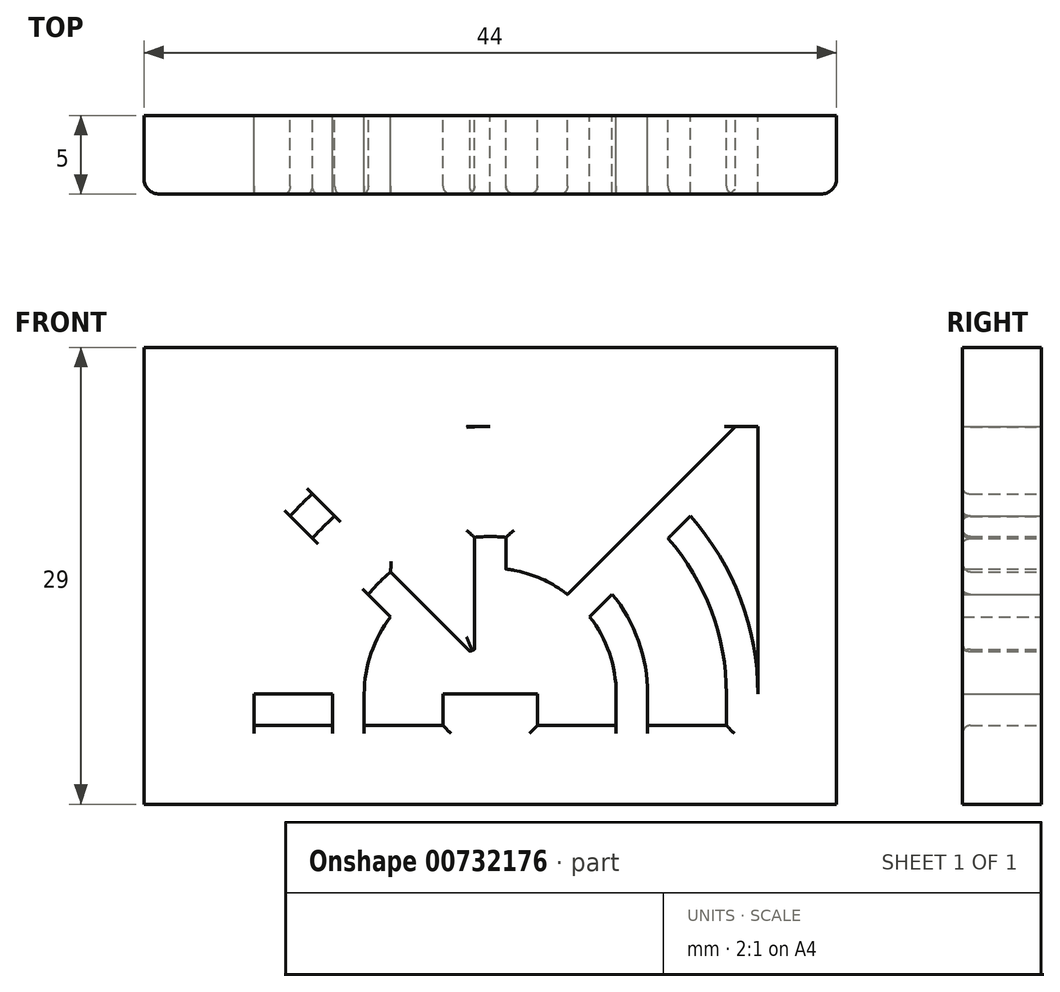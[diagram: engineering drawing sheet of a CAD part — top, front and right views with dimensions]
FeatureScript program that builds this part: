
annotation { "Feature Type Name" : "Feature", "Feature Type Description" : "" }
export const myFeature = defineFeature(function(context is Context, id is Id, definition is map)
    precondition{}
    {
        {
            var Q0;
            Q0=qCreatedBy(makeId("Front.planeOp"),FACE);
            var sketch = newSketch(context, id + "F0", { "sketchPlane" : qUnion([Q0])});
            skLineSegment(sketch, "E0.bottom", {"start": v(44, 28.95) * mm, "end": v(0, 28.95) * mm});
            skLineSegment(sketch, "E0.top", {"start": v(44, -0.05) * mm, "end": v(0, -0.05) * mm});
            skLineSegment(sketch, "E0.left", {"start": v(44, 28.95) * mm, "end": v(44, -0.05) * mm});
            skLineSegment(sketch, "E0.right", {"start": v(0, 28.95) * mm, "end": v(0, -0.05) * mm});
            skPoint(sketch, "E1.middle", {"position": v(22, 14.45) * mm});
            skLineSegment(sketch, "E2", {"start": v(5, 6.95) * mm, "end": v(39, 6.95) * mm});
            skPoint(sketch, "E3", {"position": v(22, 6.95) * mm});
            skArc(sketch, "E4", {"start": v(5, 6.95) * mm, "mid": v(22, 23.95) * mm, "end": v(39, 6.95) * mm});
            skArc(sketch, "E5", {"start": v(7, 6.95) * mm, "mid": v(22, 21.95) * mm, "end": v(37, 6.95) * mm});
            skArc(sketch, "E6", {"start": v(12, 6.95) * mm, "mid": v(22, 16.95) * mm, "end": v(32, 6.95) * mm});
            skArc(sketch, "E7", {"start": v(14, 6.95) * mm, "mid": v(22, 14.95) * mm, "end": v(30, 6.95) * mm});
            skArc(sketch, "E8", {"start": v(19, 6.95) * mm, "mid": v(22, 9.95) * mm, "end": v(25, 6.95) * mm});
            skLineSegment(sketch, "E9", {"start": v(7, 6.95) * mm, "end": v(7, 4.95) * mm});
            skLineSegment(sketch, "E10", {"start": v(12, 6.95) * mm, "end": v(12, 4.95) * mm});
            skLineSegment(sketch, "E11", {"start": v(14, 6.95) * mm, "end": v(14, 4.95) * mm});
            skLineSegment(sketch, "E12", {"start": v(19, 6.95) * mm, "end": v(19, 4.95) * mm});
            skLineSegment(sketch, "E13", {"start": v(25, 6.95) * mm, "end": v(25, 4.95) * mm});
            skLineSegment(sketch, "E14", {"start": v(30, 6.95) * mm, "end": v(30, 4.95) * mm});
            skLineSegment(sketch, "E15", {"start": v(32, 6.95) * mm, "end": v(32, 4.95) * mm});
            skLineSegment(sketch, "E16", {"start": v(37, 6.95) * mm, "end": v(37, 4.95) * mm});
            skLineSegment(sketch, "E17", {"start": v(37.59, 23.95) * mm, "end": v(23.3, 9.66) * mm});
            skLineSegment(sketch, "E18", {"start": v(39, 22.53) * mm, "end": v(24.7, 8.24) * mm});
            skLineSegment(sketch, "E19", {"start": v(21, 23.92) * mm, "end": v(21, 9.78) * mm});
            skLineSegment(sketch, "E20", {"start": v(23, 23.92) * mm, "end": v(23, 9.78) * mm});
            skLineSegment(sketch, "E21", {"start": v(6.41, 23.95) * mm, "end": v(20.7, 9.66) * mm});
            skLineSegment(sketch, "E22", {"start": v(5, 22.53) * mm, "end": v(19.3, 8.24) * mm});
            skLineSegment(sketch, "E23", {"start": v(5, 23.95) * mm, "end": v(39, 23.95) * mm});
            skLineSegment(sketch, "E24", {"start": v(5, 23.95) * mm, "end": v(5, 4.95) * mm});
            skLineSegment(sketch, "E25", {"start": v(39, 23.95) * mm, "end": v(39, 4.95) * mm});
            skLineSegment(sketch, "E26", {"start": v(5, 4.95) * mm, "end": v(39, 4.95) * mm});
            skLineSegment(sketch, "E27", {"start": v(21, 23.87) * mm, "end": v(21, 23.95) * mm});
            skLineSegment(sketch, "E28", {"start": v(23, 23.86) * mm, "end": v(23, 23.95) * mm});
            skSolve(sketch);
        }
        {
            var Q0;
            {var subQ5=sQuery(id+"F0.wireOp",EDGE,"E27");var subQ7=sQuery(id+"F0.wireOp",EDGE,"E4");var subQ11=makeQuery(id+"F0.imprint","INTERSECT",VERTEX,{"derivedFrom":[subQ7,subQ5]});Q0=makeQuery(id+"F0.imprint","IMPRINT",FACE,{"disambiguationData":[TD([[makeQuery(id+"F0.imprint","IMPRINT",EDGE,{"disambiguationData":[TD([[subQ11,-1.0]])],"derivedFrom":subQ7}),-1.0]])]});}
            var Q1;
            {var subQ0=sQuery(id+"F0.wireOp",EDGE,"E19");var subQ1=sQuery(id+"F0.wireOp",EDGE,"E5");var subQ2=makeQuery(id+"F0.imprint","INTERSECT",VERTEX,{"derivedFrom":[subQ1,subQ0]});Q1=makeQuery(id+"F0.imprint","IMPRINT",FACE,{"disambiguationData":[TD([[makeQuery(id+"F0.imprint","IMPRINT",EDGE,{"disambiguationData":[TD([[subQ2,-1.0]])],"derivedFrom":subQ1}),-1.0]])]});}
            var Q2;
            Q2=makeQuery(id+"F0.imprint","IMPRINT",FACE,{"disambiguationData":[TD([[makeQuery(id+"F0.imprint","IMPRINT",EDGE,{"derivedFrom":sQuery(id+"F0.wireOp",EDGE,"E0.bottom")}),1.0]])]});
            var Q3;
            {var subQ5=sQuery(id+"F0.wireOp",EDGE,"E22");var subQ7=sQuery(id+"F0.wireOp",EDGE,"E4");var subQ8=makeQuery(id+"F0.imprint","INTERSECT",VERTEX,{"derivedFrom":[subQ7,subQ5]});Q3=makeQuery(id+"F0.imprint","IMPRINT",FACE,{"disambiguationData":[TD([[makeQuery(id+"F0.imprint","IMPRINT",EDGE,{"disambiguationData":[TD([[subQ8,-1.0]])],"derivedFrom":subQ7}),1.0]])]});}
            var Q4;
            {var subQ0=sQuery(id+"F0.wireOp",EDGE,"E22");var subQ1=sQuery(id+"F0.wireOp",EDGE,"E4");var subQ2=makeQuery(id+"F0.imprint","INTERSECT",VERTEX,{"derivedFrom":[subQ1,subQ0]});Q4=makeQuery(id+"F0.imprint","IMPRINT",FACE,{"disambiguationData":[TD([[makeQuery(id+"F0.imprint","IMPRINT",EDGE,{"disambiguationData":[TD([[subQ2,-1.0]])],"derivedFrom":subQ1}),-1.0]])]});}
            var Q5;
            {var subQ0=sQuery(id+"F0.wireOp",EDGE,"E21");var subQ1=sQuery(id+"F0.wireOp",EDGE,"E4");var subQ2=makeQuery(id+"F0.imprint","INTERSECT",VERTEX,{"derivedFrom":[subQ1,subQ0]});Q5=makeQuery(id+"F0.imprint","IMPRINT",FACE,{"disambiguationData":[TD([[makeQuery(id+"F0.imprint","IMPRINT",EDGE,{"disambiguationData":[TD([[subQ2,-1.0]])],"derivedFrom":subQ1}),-1.0]])]});}
            var Q6;
            {var subQ0=sQuery(id+"F0.wireOp",EDGE,"E4");var subQ5=sQuery(id+"F0.wireOp",EDGE,"E22");var subQ6=makeQuery(id+"F0.imprint","INTERSECT",VERTEX,{"derivedFrom":[subQ0,subQ5]});Q6=makeQuery(id+"F0.imprint","IMPRINT",FACE,{"disambiguationData":[TD([[makeQuery(id+"F0.imprint","IMPRINT",EDGE,{"disambiguationData":[TD([[subQ6,-1.0]])],"derivedFrom":subQ5}),-1.0]])]});}
            var Q7;
            {var subQ3=sQuery(id+"F0.wireOp",EDGE,"E9");Q7=makeQuery(id+"F0.imprint","IMPRINT",FACE,{"disambiguationData":[TD([[makeQuery(id+"F0.imprint","IMPRINT",EDGE,{"derivedFrom":subQ3}),-1.0]])]});}
            var Q8;
            {var subQ0=sQuery(id+"F0.wireOp",EDGE,"E10");Q8=makeQuery(id+"F0.imprint","IMPRINT",FACE,{"disambiguationData":[TD([[makeQuery(id+"F0.imprint","IMPRINT",EDGE,{"derivedFrom":subQ0}),1.0]])]});}
            var Q9;
            {var subQ0=sQuery(id+"F0.wireOp",EDGE,"E6");var subQ5=sQuery(id+"F0.wireOp",EDGE,"E22");var subQ6=makeQuery(id+"F0.imprint","INTERSECT",VERTEX,{"derivedFrom":[subQ0,subQ5]});Q9=makeQuery(id+"F0.imprint","IMPRINT",FACE,{"disambiguationData":[TD([[makeQuery(id+"F0.imprint","IMPRINT",EDGE,{"disambiguationData":[TD([[subQ6,-1.0]])],"derivedFrom":subQ5}),-1.0]])]});}
            var Q10;
            {var subQ0=sQuery(id+"F0.wireOp",EDGE,"E22");var subQ1=sQuery(id+"F0.wireOp",EDGE,"E6");var subQ2=makeQuery(id+"F0.imprint","INTERSECT",VERTEX,{"derivedFrom":[subQ1,subQ0]});Q10=makeQuery(id+"F0.imprint","IMPRINT",FACE,{"disambiguationData":[TD([[makeQuery(id+"F0.imprint","IMPRINT",EDGE,{"disambiguationData":[TD([[subQ2,-1.0]])],"derivedFrom":subQ1}),-1.0]])]});}
            var Q11;
            {var subQ0=sQuery(id+"F0.wireOp",EDGE,"E22");var subQ1=sQuery(id+"F0.wireOp",EDGE,"E5");var subQ2=makeQuery(id+"F0.imprint","INTERSECT",VERTEX,{"derivedFrom":[subQ1,subQ0]});Q11=makeQuery(id+"F0.imprint","IMPRINT",FACE,{"disambiguationData":[TD([[makeQuery(id+"F0.imprint","IMPRINT",EDGE,{"disambiguationData":[TD([[subQ2,-1.0]])],"derivedFrom":subQ1}),-1.0]])]});}
            var Q12;
            {var subQ0=sQuery(id+"F0.wireOp",EDGE,"E21");var subQ1=sQuery(id+"F0.wireOp",EDGE,"E6");var subQ2=makeQuery(id+"F0.imprint","INTERSECT",VERTEX,{"derivedFrom":[subQ1,subQ0]});Q12=makeQuery(id+"F0.imprint","IMPRINT",FACE,{"disambiguationData":[TD([[makeQuery(id+"F0.imprint","IMPRINT",EDGE,{"disambiguationData":[TD([[subQ2,-1.0]])],"derivedFrom":subQ1}),-1.0]])]});}
            var Q13;
            {var subQ0=sQuery(id+"F0.wireOp",EDGE,"E28");var subQ7=sQuery(id+"F0.wireOp",EDGE,"E4");var subQ9=makeQuery(id+"F0.imprint","INTERSECT",VERTEX,{"derivedFrom":[subQ7,subQ0]});Q13=makeQuery(id+"F0.imprint","IMPRINT",FACE,{"disambiguationData":[TD([[makeQuery(id+"F0.imprint","IMPRINT",EDGE,{"disambiguationData":[TD([[subQ9,-1.0]])],"derivedFrom":subQ7}),-1.0]])]});}
            var Q14;
            {var subQ1=sQuery(id+"F0.wireOp",EDGE,"E17");var subQ5=sQuery(id+"F0.wireOp",EDGE,"E4");var subQ6=makeQuery(id+"F0.imprint","INTERSECT",VERTEX,{"derivedFrom":[subQ5,subQ1]});Q14=makeQuery(id+"F0.imprint","IMPRINT",FACE,{"disambiguationData":[TD([[makeQuery(id+"F0.imprint","IMPRINT",EDGE,{"disambiguationData":[TD([[subQ6,-1.0]])],"derivedFrom":subQ5}),1.0]])]});}
            var Q15;
            {var subQ0=sQuery(id+"F0.wireOp",EDGE,"E17");var subQ1=sQuery(id+"F0.wireOp",EDGE,"E4");var subQ2=makeQuery(id+"F0.imprint","INTERSECT",VERTEX,{"derivedFrom":[subQ1,subQ0]});Q15=makeQuery(id+"F0.imprint","IMPRINT",FACE,{"disambiguationData":[TD([[makeQuery(id+"F0.imprint","IMPRINT",EDGE,{"disambiguationData":[TD([[subQ2,-1.0]])],"derivedFrom":subQ1}),-1.0]])]});}
            var Q16;
            {var subQ0=sQuery(id+"F0.wireOp",EDGE,"E17");var subQ1=sQuery(id+"F0.wireOp",EDGE,"E5");var subQ2=makeQuery(id+"F0.imprint","INTERSECT",VERTEX,{"derivedFrom":[subQ1,subQ0]});Q16=makeQuery(id+"F0.imprint","IMPRINT",FACE,{"disambiguationData":[TD([[makeQuery(id+"F0.imprint","IMPRINT",EDGE,{"disambiguationData":[TD([[subQ2,-1.0]])],"derivedFrom":subQ1}),-1.0]])]});}
            var Q17;
            {var subQ0=sQuery(id+"F0.wireOp",EDGE,"E4");var subQ5=sQuery(id+"F0.wireOp",EDGE,"E18");var subQ7=makeQuery(id+"F0.imprint","INTERSECT",VERTEX,{"derivedFrom":[subQ0,subQ5]});Q17=makeQuery(id+"F0.imprint","IMPRINT",FACE,{"disambiguationData":[TD([[makeQuery(id+"F0.imprint","IMPRINT",EDGE,{"disambiguationData":[TD([[subQ7,-1.0]])],"derivedFrom":subQ5}),1.0]])]});}
            var Q18;
            {var subQ3=sQuery(id+"F0.wireOp",EDGE,"E16");Q18=makeQuery(id+"F0.imprint","IMPRINT",FACE,{"disambiguationData":[TD([[makeQuery(id+"F0.imprint","IMPRINT",EDGE,{"derivedFrom":subQ3}),1.0]])]});}
            var Q19;
            {var subQ0=sQuery(id+"F0.wireOp",EDGE,"E6");var subQ5=sQuery(id+"F0.wireOp",EDGE,"E18");var subQ6=makeQuery(id+"F0.imprint","INTERSECT",VERTEX,{"derivedFrom":[subQ0,subQ5]});Q19=makeQuery(id+"F0.imprint","IMPRINT",FACE,{"disambiguationData":[TD([[makeQuery(id+"F0.imprint","IMPRINT",EDGE,{"disambiguationData":[TD([[subQ6,-1.0]])],"derivedFrom":subQ5}),1.0]])]});}
            var Q20;
            {var subQ0=sQuery(id+"F0.wireOp",EDGE,"E17");var subQ1=sQuery(id+"F0.wireOp",EDGE,"E6");var subQ2=makeQuery(id+"F0.imprint","INTERSECT",VERTEX,{"derivedFrom":[subQ1,subQ0]});Q20=makeQuery(id+"F0.imprint","IMPRINT",FACE,{"disambiguationData":[TD([[makeQuery(id+"F0.imprint","IMPRINT",EDGE,{"disambiguationData":[TD([[subQ2,-1.0]])],"derivedFrom":subQ1}),-1.0]])]});}
            var Q21;
            {var subQ0=sQuery(id+"F0.wireOp",EDGE,"E20");var subQ1=sQuery(id+"F0.wireOp",EDGE,"E6");var subQ2=makeQuery(id+"F0.imprint","INTERSECT",VERTEX,{"derivedFrom":[subQ1,subQ0]});Q21=makeQuery(id+"F0.imprint","IMPRINT",FACE,{"disambiguationData":[TD([[makeQuery(id+"F0.imprint","IMPRINT",EDGE,{"disambiguationData":[TD([[subQ2,-1.0]])],"derivedFrom":subQ1}),-1.0]])]});}
            var Q22;
            {var subQ0=sQuery(id+"F0.wireOp",EDGE,"E27");var subQ1=sQuery(id+"F0.wireOp",EDGE,"E4");var subQ2=makeQuery(id+"F0.imprint","INTERSECT",VERTEX,{"derivedFrom":[subQ1,subQ0]});Q22=makeQuery(id+"F0.imprint","IMPRINT",FACE,{"disambiguationData":[TD([[makeQuery(id+"F0.imprint","IMPRINT",EDGE,{"disambiguationData":[TD([[subQ2,-1.0]])],"derivedFrom":subQ1}),1.0]])]});}
            var Q23;
            {var subQ0=sQuery(id+"F0.wireOp",EDGE,"E23");var subQ1=sQuery(id+"F0.wireOp",EDGE,"E4");var subQ2=makeQuery(id+"F0.imprint","INTERSECT",VERTEX,{"derivedFrom":[subQ1,subQ0]});Q23=makeQuery(id+"F0.imprint","IMPRINT",FACE,{"disambiguationData":[TD([[makeQuery(id+"F0.imprint","IMPRINT",EDGE,{"disambiguationData":[TD([[subQ2,-1.0]])],"derivedFrom":subQ1}),1.0]])]});}
            var Q24;
            {var subQ2=sQuery(id+"F0.wireOp",EDGE,"E14");Q24=makeQuery(id+"F0.imprint","IMPRINT",FACE,{"disambiguationData":[TD([[makeQuery(id+"F0.imprint","IMPRINT",EDGE,{"derivedFrom":subQ2}),1.0]])]});}
            var Q25;
            {var subQ0=sQuery(id+"F0.wireOp",EDGE,"E19");var subQ1=sQuery(id+"F0.wireOp",EDGE,"E6");var subQ2=makeQuery(id+"F0.imprint","INTERSECT",VERTEX,{"derivedFrom":[subQ1,subQ0]});Q25=makeQuery(id+"F0.imprint","IMPRINT",FACE,{"disambiguationData":[TD([[makeQuery(id+"F0.imprint","IMPRINT",EDGE,{"disambiguationData":[TD([[subQ2,-1.0]])],"derivedFrom":subQ1}),-1.0]])]});}
            var Q26;
            {var subQ0=sQuery(id+"F0.wireOp",EDGE,"E19");var subQ1=sQuery(id+"F0.wireOp",EDGE,"E7");var subQ2=makeQuery(id+"F0.imprint","INTERSECT",VERTEX,{"derivedFrom":[subQ1,subQ0]});Q26=makeQuery(id+"F0.imprint","IMPRINT",FACE,{"disambiguationData":[TD([[makeQuery(id+"F0.imprint","IMPRINT",EDGE,{"disambiguationData":[TD([[subQ2,-1.0]])],"derivedFrom":subQ1}),-1.0]])]});}
            var Q27;
            {var subQ0=sQuery(id+"F0.wireOp",EDGE,"E17");var subQ1=sQuery(id+"F0.wireOp",EDGE,"E7");var subQ2=makeQuery(id+"F0.imprint","INTERSECT",VERTEX,{"derivedFrom":[subQ1,subQ0]});Q27=makeQuery(id+"F0.imprint","IMPRINT",FACE,{"disambiguationData":[TD([[makeQuery(id+"F0.imprint","IMPRINT",EDGE,{"disambiguationData":[TD([[subQ2,-1.0]])],"derivedFrom":subQ1}),-1.0]])]});}
            var Q28;
            {var subQ0=sQuery(id+"F0.wireOp",EDGE,"E22");var subQ1=sQuery(id+"F0.wireOp",EDGE,"E7");var subQ2=makeQuery(id+"F0.imprint","INTERSECT",VERTEX,{"derivedFrom":[subQ1,subQ0]});Q28=makeQuery(id+"F0.imprint","IMPRINT",FACE,{"disambiguationData":[TD([[makeQuery(id+"F0.imprint","IMPRINT",EDGE,{"disambiguationData":[TD([[subQ2,-1.0]])],"derivedFrom":subQ1}),-1.0]])]});}
            var Q29;
            {var subQ0=sQuery(id+"F0.wireOp",EDGE,"E8");var subQ2=makeQuery(id+"F0.imprint","INTERSECT",VERTEX,{"derivedFrom":[subQ0,sQuery(id+"F0.wireOp",EDGE,"E21")]});Q29=makeQuery(id+"F0.imprint","IMPRINT",FACE,{"disambiguationData":[TD([[makeQuery(id+"F0.imprint","IMPRINT",EDGE,{"disambiguationData":[TD([[subQ2,1.0]])],"derivedFrom":subQ0}),-1.0]])]});}
            var Q30;
            {var subQ0=sQuery(id+"F0.wireOp",EDGE,"E12");Q30=makeQuery(id+"F0.imprint","IMPRINT",FACE,{"disambiguationData":[TD([[makeQuery(id+"F0.imprint","IMPRINT",EDGE,{"derivedFrom":subQ0}),1.0]])]});}
            extrude(context, id + "F1", {"entities" : qUnion([Q0, Q1, Q2, Q3, Q4, Q5, Q6, Q7, Q8, Q9, Q10, Q11, Q12, Q13, Q14, Q15, Q16, Q17, Q18, Q19, Q20, Q21, Q22, Q23, Q24, Q25, Q26, Q27, Q28, Q29, Q30]), "depth" : 5 * mm, "offsetDistance" : 25 * mm});
        }
        {
            var Q0;
            {var subQ0=sQuery(id+"F0.wireOp",EDGE,"E5");Q0=makeQuery(id+"F1.opExtrude","CAP_EDGE",EDGE,{"disambiguationData":[OSD([subQ0]),TDD([makeQuery(id+"F0.imprint","IMPRINT",EDGE,{"disambiguationData":[TD([[makeQuery(id+"F0.imprint","INTERSECT",VERTEX,{"derivedFrom":[subQ0,sQuery(id+"F0.wireOp",EDGE,"E22")]}),1.0]])],"derivedFrom":subQ0})])],"isStart":false});}
            var Q1;
            {var subQ0=sQuery(id+"F0.wireOp",EDGE,"E22");Q1=makeQuery(id+"F1.opExtrude","CAP_EDGE",EDGE,{"disambiguationData":[OSD([subQ0]),TDD([makeQuery(id+"F0.imprint","IMPRINT",EDGE,{"disambiguationData":[TD([[makeQuery(id+"F0.imprint","INTERSECT",VERTEX,{"derivedFrom":[sQuery(id+"F0.wireOp",EDGE,"E5"),subQ0]}),-1.0]])],"derivedFrom":subQ0})])],"isStart":false});}
            var Q2;
            {var subQ0=sQuery(id+"F0.wireOp",EDGE,"E19");Q2=makeQuery(id+"F1.opExtrude","CAP_EDGE",EDGE,{"disambiguationData":[OSD([subQ0]),TDD([makeQuery(id+"F0.imprint","IMPRINT",EDGE,{"disambiguationData":[TD([[makeQuery(id+"F0.imprint","INTERSECT",VERTEX,{"derivedFrom":[sQuery(id+"F0.wireOp",EDGE,"E5"),subQ0]}),-1.0]])],"derivedFrom":subQ0})])],"isStart":false});}
            var Q3;
            {var subQ0=sQuery(id+"F0.wireOp",EDGE,"E6");Q3=makeQuery(id+"F1.opExtrude","CAP_EDGE",EDGE,{"disambiguationData":[OSD([subQ0]),TDD([makeQuery(id+"F0.imprint","IMPRINT",EDGE,{"disambiguationData":[TD([[makeQuery(id+"F0.imprint","INTERSECT",VERTEX,{"derivedFrom":[subQ0,sQuery(id+"F0.wireOp",EDGE,"E21")]}),-1.0]])],"derivedFrom":subQ0})])],"isStart":false});}
            var Q4;
            {var subQ0=sQuery(id+"F0.wireOp",EDGE,"E5");Q4=makeQuery(id+"F1.opExtrude","CAP_EDGE",EDGE,{"disambiguationData":[OSD([subQ0]),TDD([makeQuery(id+"F0.imprint","IMPRINT",EDGE,{"disambiguationData":[TD([[makeQuery(id+"F0.imprint","INTERSECT",VERTEX,{"derivedFrom":[subQ0,sQuery(id+"F0.wireOp",EDGE,"E21")]}),-1.0]])],"derivedFrom":subQ0})])],"isStart":false});}
            var Q5;
            {var subQ0=sQuery(id+"F0.wireOp",EDGE,"E21");Q5=makeQuery(id+"F1.opExtrude","CAP_EDGE",EDGE,{"disambiguationData":[OSD([subQ0]),TDD([makeQuery(id+"F0.imprint","IMPRINT",EDGE,{"disambiguationData":[TD([[makeQuery(id+"F0.imprint","INTERSECT",VERTEX,{"derivedFrom":[sQuery(id+"F0.wireOp",EDGE,"E5"),subQ0]}),-1.0]])],"derivedFrom":subQ0})])],"isStart":false});}
            var Q6;
            {var subQ0=sQuery(id+"F0.wireOp",EDGE,"E6");Q6=makeQuery(id+"F1.opExtrude","CAP_EDGE",EDGE,{"disambiguationData":[OSD([subQ0]),TDD([makeQuery(id+"F0.imprint","IMPRINT",EDGE,{"disambiguationData":[TD([[makeQuery(id+"F0.imprint","INTERSECT",VERTEX,{"derivedFrom":[subQ0,sQuery(id+"F0.wireOp",EDGE,"E22")]}),1.0]])],"derivedFrom":subQ0})])],"isStart":false});}
            var Q7;
            {var subQ0=sQuery(id+"F0.wireOp",EDGE,"E7");Q7=makeQuery(id+"F1.opExtrude","CAP_EDGE",EDGE,{"disambiguationData":[OSD([subQ0]),TDD([makeQuery(id+"F0.imprint","IMPRINT",EDGE,{"disambiguationData":[TD([[makeQuery(id+"F0.imprint","INTERSECT",VERTEX,{"derivedFrom":[subQ0,sQuery(id+"F0.wireOp",EDGE,"E22")]}),1.0]])],"derivedFrom":subQ0})])],"isStart":false});}
            var Q8;
            Q8=makeQuery(id+"F1.opExtrude","CAP_EDGE",EDGE,{"disambiguationData":[OSD([sQuery(id+"F0.wireOp",EDGE,"E12")])],"isStart":false});
            var Q9;
            {var subQ0=sQuery(id+"F0.wireOp",EDGE,"E8");Q9=makeQuery(id+"F1.opExtrude","CAP_EDGE",EDGE,{"disambiguationData":[OSD([subQ0]),TDD([makeQuery(id+"F0.imprint","IMPRINT",EDGE,{"disambiguationData":[TD([[makeQuery(id+"F0.imprint","INTERSECT",VERTEX,{"derivedFrom":[subQ0,sQuery(id+"F0.wireOp",EDGE,"E22")]}),1.0]])],"derivedFrom":subQ0})])],"isStart":false});}
            var Q10;
            {var subQ0=sQuery(id+"F0.wireOp",EDGE,"E22");Q10=makeQuery(id+"F1.opExtrude","CAP_EDGE",EDGE,{"disambiguationData":[OSD([subQ0]),TDD([makeQuery(id+"F0.imprint","IMPRINT",EDGE,{"disambiguationData":[TD([[makeQuery(id+"F0.imprint","INTERSECT",VERTEX,{"derivedFrom":[sQuery(id+"F0.wireOp",EDGE,"E8"),subQ0]}),1.0]])],"derivedFrom":subQ0})])],"isStart":false});}
            var Q11;
            {var subQ0=sQuery(id+"F0.wireOp",EDGE,"E4");Q11=makeQuery(id+"F1.opExtrude","CAP_EDGE",EDGE,{"disambiguationData":[OSD([subQ0]),TDD([makeQuery(id+"F0.imprint","IMPRINT",EDGE,{"disambiguationData":[TD([[makeQuery(id+"F0.imprint","INTERSECT",VERTEX,{"derivedFrom":[subQ0,sQuery(id+"F0.wireOp",EDGE,"E21")]}),-1.0]])],"derivedFrom":subQ0})])],"isStart":false});}
            var Q12;
            {var subQ0=sQuery(id+"F0.wireOp",EDGE,"E23");Q12=makeQuery(id+"F1.opExtrude","CAP_EDGE",EDGE,{"disambiguationData":[OSD([subQ0]),TDD([makeQuery(id+"F0.imprint","IMPRINT",EDGE,{"disambiguationData":[TD([[makeQuery(id+"F0.imprint","INTERSECT",VERTEX,{"derivedFrom":[sQuery(id+"F0.wireOp",EDGE,"E21"),subQ0]}),-1.0]])],"derivedFrom":subQ0})])],"isStart":false});}
            var Q13;
            {var subQ0=sQuery(id+"F0.wireOp",EDGE,"E21");Q13=makeQuery(id+"F1.opExtrude","CAP_EDGE",EDGE,{"disambiguationData":[OSD([subQ0]),TDD([makeQuery(id+"F0.imprint","IMPRINT",EDGE,{"disambiguationData":[TD([[makeQuery(id+"F0.imprint","INTERSECT",VERTEX,{"derivedFrom":[subQ0,sQuery(id+"F0.wireOp",EDGE,"E23")]}),-1.0]])],"derivedFrom":subQ0})])],"isStart":false});}
            var Q14;
            {var subQ0=sQuery(id+"F0.wireOp",EDGE,"E21");Q14=makeQuery(id+"F1.opExtrude","CAP_EDGE",EDGE,{"disambiguationData":[OSD([subQ0]),TDD([makeQuery(id+"F0.imprint","IMPRINT",EDGE,{"disambiguationData":[TD([[makeQuery(id+"F0.imprint","INTERSECT",VERTEX,{"derivedFrom":[sQuery(id+"F0.wireOp",EDGE,"E8"),subQ0]}),1.0]])],"derivedFrom":subQ0})])],"isStart":false});}
            var Q15;
            {var subQ0=sQuery(id+"F0.wireOp",EDGE,"E7");Q15=makeQuery(id+"F1.opExtrude","CAP_EDGE",EDGE,{"disambiguationData":[OSD([subQ0]),TDD([makeQuery(id+"F0.imprint","IMPRINT",EDGE,{"disambiguationData":[TD([[makeQuery(id+"F0.imprint","INTERSECT",VERTEX,{"derivedFrom":[subQ0,sQuery(id+"F0.wireOp",EDGE,"E21")]}),-1.0]])],"derivedFrom":subQ0})])],"isStart":false});}
            var Q16;
            {var subQ0=sQuery(id+"F0.wireOp",EDGE,"E19");Q16=makeQuery(id+"F1.opExtrude","CAP_EDGE",EDGE,{"disambiguationData":[OSD([subQ0]),TDD([makeQuery(id+"F0.imprint","IMPRINT",EDGE,{"disambiguationData":[TD([[makeQuery(id+"F0.imprint","INTERSECT",VERTEX,{"derivedFrom":[sQuery(id+"F0.wireOp",EDGE,"E8"),subQ0]}),1.0]])],"derivedFrom":subQ0})])],"isStart":false});}
            var Q17;
            {var subQ0=sQuery(id+"F0.wireOp",EDGE,"E20");Q17=makeQuery(id+"F1.opExtrude","CAP_EDGE",EDGE,{"disambiguationData":[OSD([subQ0]),TDD([makeQuery(id+"F0.imprint","IMPRINT",EDGE,{"disambiguationData":[TD([[makeQuery(id+"F0.imprint","INTERSECT",VERTEX,{"derivedFrom":[sQuery(id+"F0.wireOp",EDGE,"E5"),subQ0]}),-1.0]])],"derivedFrom":subQ0})])],"isStart":false});}
            var Q18;
            {var subQ0=sQuery(id+"F0.wireOp",EDGE,"E5");Q18=makeQuery(id+"F1.opExtrude","CAP_EDGE",EDGE,{"disambiguationData":[OSD([subQ0]),TDD([makeQuery(id+"F0.imprint","IMPRINT",EDGE,{"disambiguationData":[TD([[makeQuery(id+"F0.imprint","INTERSECT",VERTEX,{"derivedFrom":[subQ0,sQuery(id+"F0.wireOp",EDGE,"E20")]}),-1.0]])],"derivedFrom":subQ0})])],"isStart":false});}
            var Q19;
            {var subQ0=sQuery(id+"F0.wireOp",EDGE,"E23");Q19=makeQuery(id+"F1.opExtrude","CAP_EDGE",EDGE,{"disambiguationData":[OSD([subQ0]),TDD([makeQuery(id+"F0.imprint","IMPRINT",EDGE,{"disambiguationData":[TD([[makeQuery(id+"F0.imprint","INTERSECT",VERTEX,{"derivedFrom":[sQuery(id+"F0.wireOp",EDGE,"E17"),subQ0]}),1.0]])],"derivedFrom":subQ0})])],"isStart":false});}
            var Q20;
            {var subQ0=sQuery(id+"F0.wireOp",EDGE,"E17");Q20=makeQuery(id+"F1.opExtrude","CAP_EDGE",EDGE,{"disambiguationData":[OSD([subQ0]),TDD([makeQuery(id+"F0.imprint","IMPRINT",EDGE,{"disambiguationData":[TD([[makeQuery(id+"F0.imprint","INTERSECT",VERTEX,{"derivedFrom":[subQ0,sQuery(id+"F0.wireOp",EDGE,"E23")]}),-1.0]])],"derivedFrom":subQ0})])],"isStart":false});}
            var Q21;
            {var subQ0=sQuery(id+"F0.wireOp",EDGE,"E4");Q21=makeQuery(id+"F1.opExtrude","CAP_EDGE",EDGE,{"disambiguationData":[OSD([subQ0]),TDD([makeQuery(id+"F0.imprint","IMPRINT",EDGE,{"disambiguationData":[TD([[makeQuery(id+"F0.imprint","INTERSECT",VERTEX,{"derivedFrom":[subQ0,sQuery(id+"F0.wireOp",EDGE,"E28")]}),-1.0]])],"derivedFrom":subQ0})])],"isStart":false});}
            var Q22;
            {var subQ0=sQuery(id+"F0.wireOp",EDGE,"E22");Q22=makeQuery(id+"F1.opExtrude","CAP_EDGE",EDGE,{"disambiguationData":[OSD([subQ0]),TDD([makeQuery(id+"F0.imprint","IMPRINT",EDGE,{"disambiguationData":[TD([[makeQuery(id+"F0.imprint","INTERSECT",VERTEX,{"derivedFrom":[subQ0,sQuery(id+"F0.wireOp",EDGE,"E24")]}),-1.0]])],"derivedFrom":subQ0})])],"isStart":false});}
            var Q23;
            {var subQ0=sQuery(id+"F0.wireOp",EDGE,"E17");Q23=makeQuery(id+"F1.opExtrude","CAP_EDGE",EDGE,{"disambiguationData":[OSD([subQ0]),TDD([makeQuery(id+"F0.imprint","IMPRINT",EDGE,{"disambiguationData":[TD([[makeQuery(id+"F0.imprint","INTERSECT",VERTEX,{"derivedFrom":[sQuery(id+"F0.wireOp",EDGE,"E5"),subQ0]}),-1.0]])],"derivedFrom":subQ0})])],"isStart":false});}
            var Q24;
            {var subQ0=sQuery(id+"F0.wireOp",EDGE,"E6");Q24=makeQuery(id+"F1.opExtrude","CAP_EDGE",EDGE,{"disambiguationData":[OSD([subQ0]),TDD([makeQuery(id+"F0.imprint","IMPRINT",EDGE,{"disambiguationData":[TD([[makeQuery(id+"F0.imprint","INTERSECT",VERTEX,{"derivedFrom":[subQ0,sQuery(id+"F0.wireOp",EDGE,"E20")]}),-1.0]])],"derivedFrom":subQ0})])],"isStart":false});}
            var Q25;
            {var subQ0=sQuery(id+"F0.wireOp",EDGE,"E20");Q25=makeQuery(id+"F1.opExtrude","CAP_EDGE",EDGE,{"disambiguationData":[OSD([subQ0]),TDD([makeQuery(id+"F0.imprint","IMPRINT",EDGE,{"disambiguationData":[TD([[makeQuery(id+"F0.imprint","INTERSECT",VERTEX,{"derivedFrom":[sQuery(id+"F0.wireOp",EDGE,"E8"),subQ0]}),1.0]])],"derivedFrom":subQ0})])],"isStart":false});}
            var Q26;
            {var subQ0=sQuery(id+"F0.wireOp",EDGE,"E7");Q26=makeQuery(id+"F1.opExtrude","CAP_EDGE",EDGE,{"disambiguationData":[OSD([subQ0]),TDD([makeQuery(id+"F0.imprint","IMPRINT",EDGE,{"disambiguationData":[TD([[makeQuery(id+"F0.imprint","INTERSECT",VERTEX,{"derivedFrom":[subQ0,sQuery(id+"F0.wireOp",EDGE,"E20")]}),-1.0]])],"derivedFrom":subQ0})])],"isStart":false});}
            var Q27;
            {var subQ0=sQuery(id+"F0.wireOp",EDGE,"E17");Q27=makeQuery(id+"F1.opExtrude","CAP_EDGE",EDGE,{"disambiguationData":[OSD([subQ0]),TDD([makeQuery(id+"F0.imprint","IMPRINT",EDGE,{"disambiguationData":[TD([[makeQuery(id+"F0.imprint","INTERSECT",VERTEX,{"derivedFrom":[sQuery(id+"F0.wireOp",EDGE,"E8"),subQ0]}),1.0]])],"derivedFrom":subQ0})])],"isStart":false});}
            var Q28;
            {var subQ0=sQuery(id+"F0.wireOp",EDGE,"E18");Q28=makeQuery(id+"F1.opExtrude","CAP_EDGE",EDGE,{"disambiguationData":[OSD([subQ0]),TDD([makeQuery(id+"F0.imprint","IMPRINT",EDGE,{"disambiguationData":[TD([[makeQuery(id+"F0.imprint","INTERSECT",VERTEX,{"derivedFrom":[subQ0,sQuery(id+"F0.wireOp",EDGE,"E25")]}),-1.0]])],"derivedFrom":subQ0})])],"isStart":false});}
            var Q29;
            {var subQ0=sQuery(id+"F0.wireOp",EDGE,"E18");Q29=makeQuery(id+"F1.opExtrude","CAP_EDGE",EDGE,{"disambiguationData":[OSD([subQ0]),TDD([makeQuery(id+"F0.imprint","IMPRINT",EDGE,{"disambiguationData":[TD([[makeQuery(id+"F0.imprint","INTERSECT",VERTEX,{"derivedFrom":[sQuery(id+"F0.wireOp",EDGE,"E5"),subQ0]}),-1.0]])],"derivedFrom":subQ0})])],"isStart":false});}
            var Q30;
            {var subQ0=sQuery(id+"F0.wireOp",EDGE,"E5");Q30=makeQuery(id+"F1.opExtrude","CAP_EDGE",EDGE,{"disambiguationData":[OSD([subQ0]),TDD([makeQuery(id+"F0.imprint","IMPRINT",EDGE,{"disambiguationData":[TD([[makeQuery(id+"F0.imprint","INTERSECT",VERTEX,{"derivedFrom":[subQ0,sQuery(id+"F0.wireOp",EDGE,"E18")]}),-1.0]])],"derivedFrom":subQ0})])],"isStart":false});}
            var Q31;
            Q31=makeQuery(id+"F1.opExtrude","CAP_EDGE",EDGE,{"disambiguationData":[OSD([sQuery(id+"F0.wireOp",EDGE,"E16")])],"isStart":false});
            var Q32;
            {var subQ0=sQuery(id+"F0.wireOp",EDGE,"E26");Q32=makeQuery(id+"F1.opExtrude","CAP_EDGE",EDGE,{"disambiguationData":[OSD([subQ0]),TDD([makeQuery(id+"F0.imprint","IMPRINT",EDGE,{"disambiguationData":[TD([[makeQuery(id+"F0.imprint","INTERSECT",VERTEX,{"derivedFrom":[sQuery(id+"F0.wireOp",EDGE,"E15"),subQ0]}),-1.0]])],"derivedFrom":subQ0})])],"isStart":false});}
            var Q33;
            {var subQ0=sQuery(id+"F0.wireOp",EDGE,"E6");Q33=makeQuery(id+"F1.opExtrude","CAP_EDGE",EDGE,{"disambiguationData":[OSD([subQ0]),TDD([makeQuery(id+"F0.imprint","IMPRINT",EDGE,{"disambiguationData":[TD([[makeQuery(id+"F0.imprint","INTERSECT",VERTEX,{"derivedFrom":[subQ0,sQuery(id+"F0.wireOp",EDGE,"E18")]}),-1.0]])],"derivedFrom":subQ0})])],"isStart":false});}
            var Q34;
            {var subQ0=sQuery(id+"F0.wireOp",EDGE,"E7");Q34=makeQuery(id+"F1.opExtrude","CAP_EDGE",EDGE,{"disambiguationData":[OSD([subQ0]),TDD([makeQuery(id+"F0.imprint","IMPRINT",EDGE,{"disambiguationData":[TD([[makeQuery(id+"F0.imprint","INTERSECT",VERTEX,{"derivedFrom":[subQ0,sQuery(id+"F0.wireOp",EDGE,"E18")]}),-1.0]])],"derivedFrom":subQ0})])],"isStart":false});}
            var Q35;
            {var subQ0=sQuery(id+"F0.wireOp",EDGE,"E26");Q35=makeQuery(id+"F1.opExtrude","CAP_EDGE",EDGE,{"disambiguationData":[OSD([subQ0]),TDD([makeQuery(id+"F0.imprint","IMPRINT",EDGE,{"disambiguationData":[TD([[makeQuery(id+"F0.imprint","INTERSECT",VERTEX,{"derivedFrom":[sQuery(id+"F0.wireOp",EDGE,"E13"),subQ0]}),-1.0]])],"derivedFrom":subQ0})])],"isStart":false});}
            var Q36;
            {var subQ0=sQuery(id+"F0.wireOp",EDGE,"E18");Q36=makeQuery(id+"F1.opExtrude","CAP_EDGE",EDGE,{"disambiguationData":[OSD([subQ0]),TDD([makeQuery(id+"F0.imprint","IMPRINT",EDGE,{"disambiguationData":[TD([[makeQuery(id+"F0.imprint","INTERSECT",VERTEX,{"derivedFrom":[sQuery(id+"F0.wireOp",EDGE,"E8"),subQ0]}),1.0]])],"derivedFrom":subQ0})])],"isStart":false});}
            var Q37;
            Q37=makeQuery(id+"F1.opExtrude","CAP_EDGE",EDGE,{"disambiguationData":[OSD([sQuery(id+"F0.wireOp",EDGE,"E13")])],"isStart":false});
            var Q38;
            {var subQ0=sQuery(id+"F0.wireOp",EDGE,"E26");Q38=makeQuery(id+"F1.opExtrude","CAP_EDGE",EDGE,{"disambiguationData":[OSD([subQ0]),TDD([makeQuery(id+"F0.imprint","IMPRINT",EDGE,{"disambiguationData":[TD([[makeQuery(id+"F0.imprint","INTERSECT",VERTEX,{"derivedFrom":[sQuery(id+"F0.wireOp",EDGE,"E11"),subQ0]}),-1.0]])],"derivedFrom":subQ0})])],"isStart":false});}
            var Q39;
            {var subQ0=sQuery(id+"F0.wireOp",EDGE,"E26");Q39=makeQuery(id+"F1.opExtrude","CAP_EDGE",EDGE,{"disambiguationData":[OSD([subQ0]),TDD([makeQuery(id+"F0.imprint","IMPRINT",EDGE,{"disambiguationData":[TD([[makeQuery(id+"F0.imprint","INTERSECT",VERTEX,{"derivedFrom":[sQuery(id+"F0.wireOp",EDGE,"E9"),subQ0]}),-1.0]])],"derivedFrom":subQ0})])],"isStart":false});}
            var Q40;
            {var subQ0=sQuery(id+"F0.wireOp",EDGE,"E8");Q40=makeQuery(id+"F1.opExtrude","CAP_EDGE",EDGE,{"disambiguationData":[OSD([subQ0]),TDD([makeQuery(id+"F0.imprint","IMPRINT",EDGE,{"disambiguationData":[TD([[makeQuery(id+"F0.imprint","INTERSECT",VERTEX,{"derivedFrom":[subQ0,sQuery(id+"F0.wireOp",EDGE,"E19")]}),1.0]])],"derivedFrom":subQ0})])],"isStart":false});}
            var Q41;
            {var subQ0=sQuery(id+"F0.wireOp",EDGE,"E8");Q41=makeQuery(id+"F1.opExtrude","CAP_EDGE",EDGE,{"disambiguationData":[OSD([subQ0]),TDD([makeQuery(id+"F0.imprint","IMPRINT",EDGE,{"disambiguationData":[TD([[makeQuery(id+"F0.imprint","INTERSECT",VERTEX,{"derivedFrom":[subQ0,sQuery(id+"F0.wireOp",EDGE,"E17")]}),1.0]])],"derivedFrom":subQ0})])],"isStart":false});}
            var Q42;
            Q42=makeQuery(id+"F1.opExtrude","CAP_EDGE",EDGE,{"disambiguationData":[OSD([sQuery(id+"F0.wireOp",EDGE,"E28")])],"isStart":false});
            var Q43;
            Q43=makeQuery(id+"F1.opExtrude","CAP_EDGE",EDGE,{"disambiguationData":[OSD([sQuery(id+"F0.wireOp",EDGE,"E27")])],"isStart":false});
            fillet(context, id + "F2", {"entities" : qUnion([Q0, Q1, Q2, Q3, Q4, Q5, Q6, Q7, Q8, Q9, Q10, Q11, Q12, Q13, Q14, Q15, Q16, Q17, Q18, Q19, Q20, Q21, Q22, Q23, Q24, Q25, Q26, Q27, Q28, Q29, Q30, Q31, Q32, Q33, Q34, Q35, Q36, Q37, Q38, Q39, Q40, Q41, Q42, Q43]), "radius" : 0.5 * mm, "tangentPropagation" : true, "allowEdgeOverflow" : false});
        }
        {
            var Q0;
            Q0=makeQuery(id+"F1.opExtrude","CAP_EDGE",EDGE,{"disambiguationData":[OSD([sQuery(id+"F0.wireOp",EDGE,"E0.right")])],"isStart":false});
            var Q1;
            Q1=makeQuery(id+"F1.opExtrude","CAP_EDGE",EDGE,{"disambiguationData":[OSD([sQuery(id+"F0.wireOp",EDGE,"E0.left")])],"isStart":false});
            fillet(context, id + "F3", {"entities" : qUnion([Q0, Q1]), "radius" : 1 * mm, "tangentPropagation" : true, "allowEdgeOverflow" : false});
        }
    });
